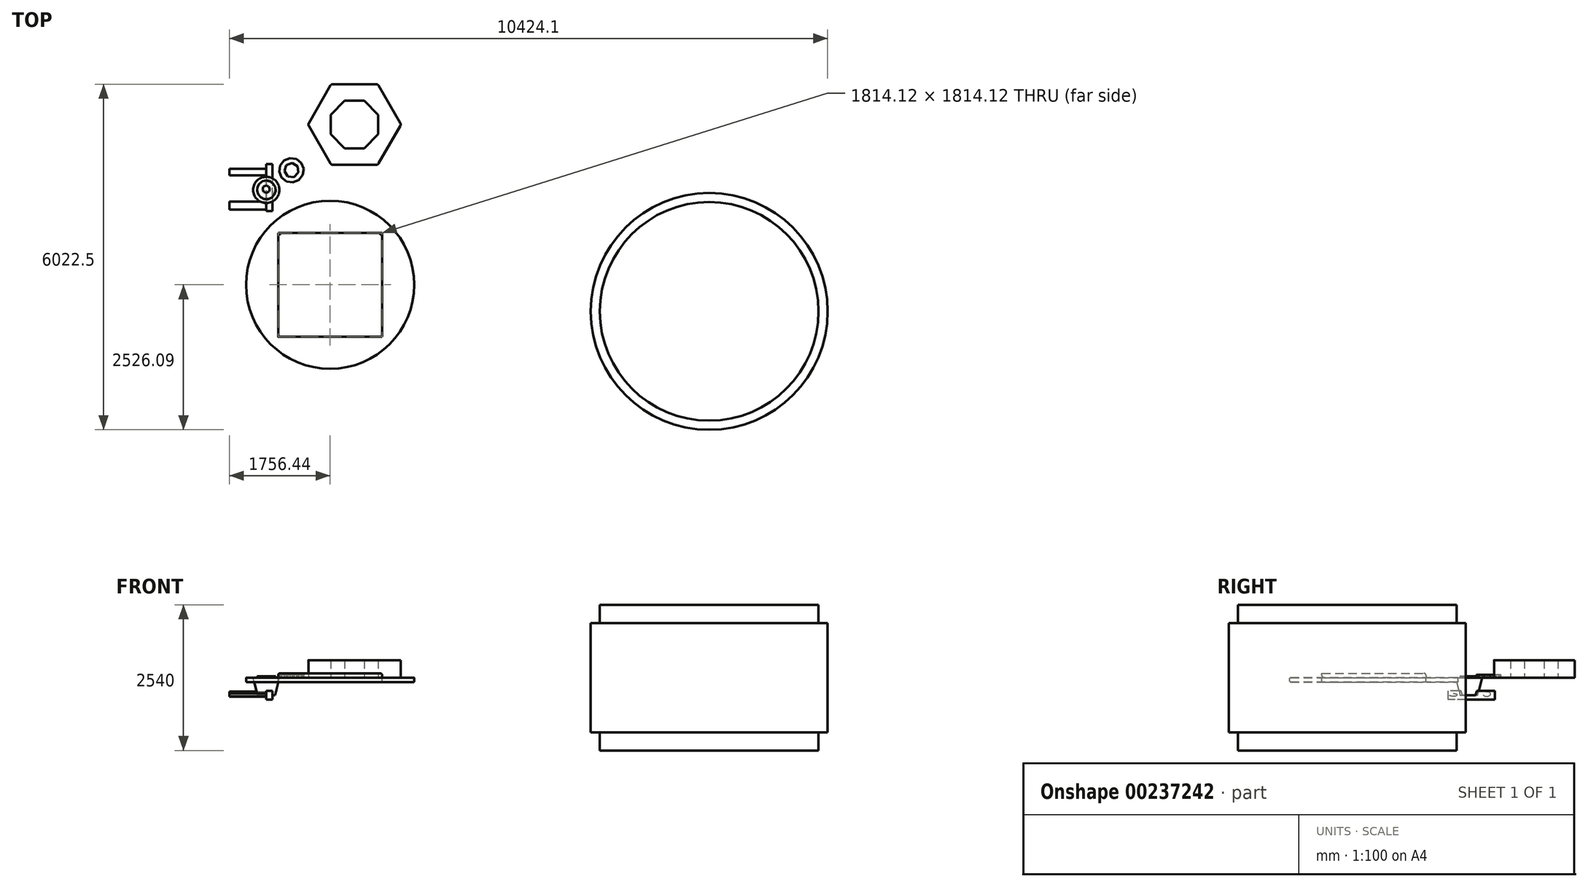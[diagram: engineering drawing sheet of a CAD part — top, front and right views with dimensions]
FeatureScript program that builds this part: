
annotation { "Feature Type Name" : "Feature", "Feature Type Description" : "" }
export const myFeature = defineFeature(function(context is Context, id is Id, definition is map)
    precondition{}
    {
        {
            var Q0;
            Q0=qCreatedBy(makeId("Top.planeOp"),FACE);
            var sketch = newSketch(context, id + "F0", { "sketchPlane" : qUnion([Q0])});
            skCircle(sketch, "E0.cCircle", {"center": v(0, 0) * mm, "radius": 162.75 * mm, "construction": true});
            skLineSegment(sketch, "E0.0", {"start": v(122.54, 107.1) * mm, "end": v(155.5, 48) * mm});
            skLineSegment(sketch, "E0.1", {"start": v(155.5, 48) * mm, "end": v(161.59, -19.4) * mm});
            skLineSegment(sketch, "E0.2", {"start": v(161.59, -19.4) * mm, "end": v(139.72, -83.45) * mm});
            skLineSegment(sketch, "E0.3", {"start": v(139.72, -83.45) * mm, "end": v(93.7, -133.07) * mm});
            skLineSegment(sketch, "E0.4", {"start": v(93.7, -133.07) * mm, "end": v(31.48, -159.67) * mm});
            skLineSegment(sketch, "E0.5", {"start": v(31.48, -159.67) * mm, "end": v(-36.19, -158.67) * mm});
            skLineSegment(sketch, "E0.6", {"start": v(-36.19, -158.67) * mm, "end": v(-97.6, -130.23) * mm});
            skLineSegment(sketch, "E0.7", {"start": v(-97.6, -130.23) * mm, "end": v(-142.13, -79.28) * mm});
            skLineSegment(sketch, "E0.8", {"start": v(-142.13, -79.28) * mm, "end": v(-162.09, -14.61) * mm});
            skLineSegment(sketch, "E0.9", {"start": v(-162.09, -14.61) * mm, "end": v(-154.02, 52.58) * mm});
            skLineSegment(sketch, "E0.10", {"start": v(-154.02, 52.58) * mm, "end": v(-119.32, 110.68) * mm});
            skLineSegment(sketch, "E0.11", {"start": v(-119.32, 110.68) * mm, "end": v(-63.99, 149.64) * mm});
            skLineSegment(sketch, "E0.12", {"start": v(-63.99, 149.64) * mm, "end": v(2.4, 162.73) * mm});
            skLineSegment(sketch, "E0.13", {"start": v(2.4, 162.73) * mm, "end": v(68.39, 147.68) * mm});
            skLineSegment(sketch, "E0.14", {"start": v(68.39, 147.68) * mm, "end": v(122.54, 107.1) * mm});
            skCircle(sketch, "E1.cCircle", {"center": v(0, 13.94) * mm, "radius": 64 * mm, "construction": true});
            skLineSegment(sketch, "E1.0", {"start": v(63.59, 21.28) * mm, "end": v(50.15, -25.83) * mm});
            skLineSegment(sketch, "E1.1", {"start": v(50.15, -25.83) * mm, "end": v(7.34, -49.65) * mm});
            skLineSegment(sketch, "E1.2", {"start": v(7.34, -49.65) * mm, "end": v(-39.77, -36.22) * mm});
            skLineSegment(sketch, "E1.3", {"start": v(-39.77, -36.22) * mm, "end": v(-63.59, 6.6) * mm});
            skLineSegment(sketch, "E1.4", {"start": v(-63.59, 6.6) * mm, "end": v(-50.15, 53.7) * mm});
            skLineSegment(sketch, "E1.5", {"start": v(-50.15, 53.7) * mm, "end": v(-7.34, 77.52) * mm});
            skLineSegment(sketch, "E1.6", {"start": v(-7.34, 77.52) * mm, "end": v(39.77, 64.09) * mm});
            skLineSegment(sketch, "E1.7", {"start": v(39.77, 64.09) * mm, "end": v(63.59, 21.28) * mm});
            skSolve(sketch);
        }
        {
            var Q0;
            Q0=makeQuery(id+"F0.imprint","IMPRINT",FACE,{"disambiguationData":[TD([[makeQuery(id+"F0.imprint","IMPRINT",EDGE,{"derivedFrom":sQuery(id+"F0.wireOp",EDGE,"E0.0")}),-1.0]])]});
            extrude(context, id + "F1", {"entities" : qUnion([Q0]), "depth" : 25.4 * mm});
        }
        {
            var Q0;
            Q0=qCreatedBy(makeId("Top.planeOp"),FACE);
            var sketch = newSketch(context, id + "F2", { "sketchPlane" : qUnion([Q0])});
            skCircle(sketch, "E2.cCircle", {"center": v(439.67, 342.5) * mm, "radius": 212.8 * mm, "construction": true});
            skLineSegment(sketch, "E2.0", {"start": v(635.27, 258.7) * mm, "end": v(567.16, 172.12) * mm});
            skLineSegment(sketch, "E2.1", {"start": v(567.16, 172.12) * mm, "end": v(464.89, 131.2) * mm});
            skLineSegment(sketch, "E2.2", {"start": v(464.89, 131.2) * mm, "end": v(355.86, 146.9) * mm});
            skLineSegment(sketch, "E2.3", {"start": v(355.86, 146.9) * mm, "end": v(269.29, 215.01) * mm});
            skLineSegment(sketch, "E2.4", {"start": v(269.29, 215.01) * mm, "end": v(228.37, 317.28) * mm});
            skLineSegment(sketch, "E2.5", {"start": v(228.37, 317.28) * mm, "end": v(244.07, 426.31) * mm});
            skLineSegment(sketch, "E2.6", {"start": v(244.07, 426.31) * mm, "end": v(312.18, 512.89) * mm});
            skLineSegment(sketch, "E2.7", {"start": v(312.18, 512.89) * mm, "end": v(414.45, 553.8) * mm});
            skLineSegment(sketch, "E2.8", {"start": v(414.45, 553.8) * mm, "end": v(523.48, 538.1) * mm});
            skLineSegment(sketch, "E2.9", {"start": v(523.48, 538.1) * mm, "end": v(610.05, 470) * mm});
            skLineSegment(sketch, "E2.10", {"start": v(610.05, 470) * mm, "end": v(650.97, 367.72) * mm});
            skLineSegment(sketch, "E2.11", {"start": v(650.97, 367.72) * mm, "end": v(635.27, 258.7) * mm});
            skCircle(sketch, "E3.cCircle", {"center": v(439.67, 342.5) * mm, "radius": 125.31 * mm, "construction": true});
            skLineSegment(sketch, "E3.0", {"start": v(558.33, 302.22) * mm, "end": v(482.16, 224.62) * mm});
            skLineSegment(sketch, "E3.1", {"start": v(482.16, 224.62) * mm, "end": v(374, 235.78) * mm});
            skLineSegment(sketch, "E3.2", {"start": v(374, 235.78) * mm, "end": v(315.28, 327.3) * mm});
            skLineSegment(sketch, "E3.3", {"start": v(315.28, 327.3) * mm, "end": v(350.23, 430.28) * mm});
            skLineSegment(sketch, "E3.4", {"start": v(350.23, 430.28) * mm, "end": v(452.53, 467.15) * mm});
            skLineSegment(sketch, "E3.5", {"start": v(452.53, 467.15) * mm, "end": v(545.14, 410.16) * mm});
            skLineSegment(sketch, "E3.6", {"start": v(545.14, 410.16) * mm, "end": v(558.33, 302.22) * mm});
            skSolve(sketch);
        }
        {
            var Q0;
            Q0=makeQuery(id+"F2.imprint","IMPRINT",FACE,{"disambiguationData":[TD([[makeQuery(id+"F2.imprint","IMPRINT",EDGE,{"derivedFrom":sQuery(id+"F2.wireOp",EDGE,"E2.0")}),-1.0]])]});
            extrude(context, id + "F3", {"entities" : qUnion([Q0]), "depth" : 51.3 * mm});
        }
        {
            var Q0;
            Q0=qCreatedBy(makeId("Top.planeOp"),FACE);
            var sketch = newSketch(context, id + "F4", { "sketchPlane" : qUnion([Q0])});
            skCircle(sketch, "E4.cCircle", {"center": v(1538.2, 1139.56) * mm, "radius": 810.97 * mm, "construction": true});
            skLineSegment(sketch, "E4.0", {"start": v(2349.16, 1139.56) * mm, "end": v(1943.68, 437.24) * mm});
            skLineSegment(sketch, "E4.1", {"start": v(1943.68, 437.24) * mm, "end": v(1132.71, 437.24) * mm});
            skLineSegment(sketch, "E4.2", {"start": v(1132.71, 437.24) * mm, "end": v(727.23, 1139.56) * mm});
            skLineSegment(sketch, "E4.3", {"start": v(727.23, 1139.56) * mm, "end": v(1132.71, 1841.87) * mm});
            skLineSegment(sketch, "E4.4", {"start": v(1132.71, 1841.87) * mm, "end": v(1943.68, 1841.87) * mm});
            skLineSegment(sketch, "E4.5", {"start": v(1943.68, 1841.87) * mm, "end": v(2349.16, 1139.56) * mm});
            skCircle(sketch, "E5.cCircle", {"center": v(1538.2, 1139.56) * mm, "radius": 447.1 * mm, "construction": true});
            skLineSegment(sketch, "E5.0", {"start": v(1951.26, 1310.66) * mm, "end": v(1951.26, 968.46) * mm});
            skLineSegment(sketch, "E5.1", {"start": v(1951.26, 968.46) * mm, "end": v(1709.3, 726.49) * mm});
            skLineSegment(sketch, "E5.2", {"start": v(1709.3, 726.49) * mm, "end": v(1367.1, 726.49) * mm});
            skLineSegment(sketch, "E5.3", {"start": v(1367.1, 726.49) * mm, "end": v(1125.13, 968.46) * mm});
            skLineSegment(sketch, "E5.4", {"start": v(1125.13, 968.46) * mm, "end": v(1125.13, 1310.66) * mm});
            skLineSegment(sketch, "E5.5", {"start": v(1125.13, 1310.66) * mm, "end": v(1367.1, 1552.63) * mm});
            skLineSegment(sketch, "E5.6", {"start": v(1367.1, 1552.63) * mm, "end": v(1709.3, 1552.63) * mm});
            skLineSegment(sketch, "E5.7", {"start": v(1709.3, 1552.63) * mm, "end": v(1951.26, 1310.66) * mm});
            skSolve(sketch);
        }
        {
            var Q0;
            Q0=makeQuery(id+"F4.imprint","IMPRINT",FACE,{"disambiguationData":[TD([[makeQuery(id+"F4.imprint","IMPRINT",EDGE,{"derivedFrom":sQuery(id+"F4.wireOp",EDGE,"E4.0")}),-1.0]])]});
            extrude(context, id + "F5", {"entities" : qUnion([Q0]), "depth" : 305.1 * mm});
        }
        {
            var Q0;
            Q0=makeQuery(id+"F5.opExtrude","SWEPT_EDGE",EDGE,{"disambiguationData":[OSD([sQuery(id+"F4.wireOp",EDGE,"E4.0"),sQuery(id+"F4.wireOp",EDGE,"E4.1")])]});
            var Q1;
            Q1=makeQuery(id+"F5.opExtrude","SWEPT_EDGE",EDGE,{"disambiguationData":[OSD([sQuery(id+"F4.wireOp",EDGE,"E4.0"),sQuery(id+"F4.wireOp",EDGE,"E4.5")])]});
            var Q2;
            Q2=makeQuery(id+"F5.opExtrude","SWEPT_EDGE",EDGE,{"disambiguationData":[OSD([sQuery(id+"F4.wireOp",EDGE,"E4.4"),sQuery(id+"F4.wireOp",EDGE,"E4.5")])]});
            var Q3;
            Q3=makeQuery(id+"F5.opExtrude","SWEPT_EDGE",EDGE,{"disambiguationData":[OSD([sQuery(id+"F4.wireOp",EDGE,"E4.3"),sQuery(id+"F4.wireOp",EDGE,"E4.4")])]});
            var Q4;
            Q4=makeQuery(id+"F5.opExtrude","SWEPT_EDGE",EDGE,{"disambiguationData":[OSD([sQuery(id+"F4.wireOp",EDGE,"E4.2"),sQuery(id+"F4.wireOp",EDGE,"E4.3")])]});
            var Q5;
            Q5=makeQuery(id+"F5.opExtrude","SWEPT_EDGE",EDGE,{"disambiguationData":[OSD([sQuery(id+"F4.wireOp",EDGE,"E4.1"),sQuery(id+"F4.wireOp",EDGE,"E4.2")])]});
            fillet(context, id + "F6", {"entities" : qUnion([Q0, Q1, Q2, Q3, Q4, Q5]), "radius" : 45.72 * mm, "tangentPropagation" : true, "allowEdgeOverflow" : false});
        }
        {
            var Q0;
            Q0=qCreatedBy(makeId("Top.planeOp"),FACE);
            var sketch = newSketch(context, id + "F7", { "sketchPlane" : qUnion([Q0])});
            skLineSegment(sketch, "E6.bottom", {"start": v(2020, -2561.6) * mm, "end": v(205.88, -2561.6) * mm});
            skLineSegment(sketch, "E6.top", {"start": v(2020, -747.49) * mm, "end": v(205.88, -747.49) * mm});
            skLineSegment(sketch, "E6.left", {"start": v(2020, -2561.6) * mm, "end": v(2020, -747.49) * mm});
            skLineSegment(sketch, "E6.right", {"start": v(205.88, -2561.6) * mm, "end": v(205.88, -747.49) * mm});
            skPoint(sketch, "E6.middle", {"position": v(1112.94, -1654.54) * mm});
            skCircle(sketch, "E7", {"center": v(1112.94, -1654.54) * mm, "radius": 1465.04 * mm});
            skSolve(sketch);
        }
        {
            var Q0;
            Q0=makeQuery(id+"F7.imprint","IMPRINT",FACE,{"disambiguationData":[TD([[makeQuery(id+"F7.imprint","IMPRINT",EDGE,{"derivedFrom":sQuery(id+"F7.wireOp",EDGE,"E6.bottom")}),1.0]])]});
            extrude(context, id + "F8", {"entities" : qUnion([Q0]), "oppositeDirection" : true, "depth" : 76.2 * mm});
        }
        {
            var Q0;
            Q0=makeQuery(id+"F7.imprint","IMPRINT",FACE,{"disambiguationData":[TD([[makeQuery(id+"F7.imprint","IMPRINT",EDGE,{"derivedFrom":sQuery(id+"F7.wireOp",EDGE,"E6.bottom")}),-1.0]])]});
            extrude(context, id + "F9", {"entities" : qUnion([Q0]), "depth" : 76.2 * mm});
        }
        {
            var Q0;
            Q0=makeQuery(id+"F9.opExtrude","CAP_EDGE",EDGE,{"disambiguationData":[OSD([sQuery(id+"F7.wireOp",EDGE,"E6.right")])],"isStart":false});
            var Q1;
            Q1=makeQuery(id+"F9.opExtrude","CAP_EDGE",EDGE,{"disambiguationData":[OSD([sQuery(id+"F7.wireOp",EDGE,"E6.left")])],"isStart":false});
            var Q2;
            Q2=makeQuery(id+"F9.opExtrude","CAP_EDGE",EDGE,{"disambiguationData":[OSD([sQuery(id+"F7.wireOp",EDGE,"E6.bottom")])],"isStart":true});
            var Q3;
            Q3=makeQuery(id+"F9.opExtrude","CAP_EDGE",EDGE,{"disambiguationData":[OSD([sQuery(id+"F7.wireOp",EDGE,"E6.top")])],"isStart":false});
            fillet(context, id + "F10", {"entities" : qUnion([Q0, Q1, Q2, Q3]), "radius" : 38.1 * mm, "tangentPropagation" : true, "allowEdgeOverflow" : false});
        }
        {
            var Q0;
            Q0=makeQuery(id+"F8.opExtrude","CAP_EDGE",EDGE,{"disambiguationData":[OSD([sQuery(id+"F7.wireOp",EDGE,"E7")])],"isStart":true});
            var Q1;
            Q1=makeQuery(id+"F8.opExtrude","CAP_EDGE",EDGE,{"disambiguationData":[OSD([sQuery(id+"F7.wireOp",EDGE,"E7")])],"isStart":false});
            fillet(context, id + "F11", {"entities" : qUnion([Q0, Q1]), "radius" : 12.7 * mm, "tangentPropagation" : true, "allowEdgeOverflow" : false});
        }
        {
            var Q0;
            Q0=qCreatedBy(makeId("Top.planeOp"),FACE);
            var sketch = newSketch(context, id + "F12", { "sketchPlane" : qUnion([Q0])});
            skCircle(sketch, "E8", {"center": v(7716.86, -2116.88) * mm, "radius": 1905 * mm});
            skCircle(sketch, "E9", {"center": v(7716.86, -2116.88) * mm, "radius": 2063.75 * mm});
            skSolve(sketch);
        }
        {
            var Q0;
            Q0=makeQuery(id+"F12.imprint","IMPRINT",FACE,{"disambiguationData":[TD([[makeQuery(id+"F12.imprint","IMPRINT",EDGE,{"derivedFrom":sQuery(id+"F12.wireOp",EDGE,"E8")}),1.0]])]});
            extrude(context, id + "F13", {"entities" : qUnion([Q0]), "endBound" : BoundingType.SYMMETRIC, "depth" : 2540 * mm});
        }
        {
            var Q0;
            Q0=makeQuery(id+"F12.imprint","IMPRINT",FACE,{"disambiguationData":[TD([[makeQuery(id+"F12.imprint","IMPRINT",EDGE,{"derivedFrom":sQuery(id+"F12.wireOp",EDGE,"E8")}),-1.0]])]});
            extrude(context, id + "F14", {"entities" : qUnion([Q0]), "operationType" : NewBodyOperationType.ADD, "endBound" : BoundingType.SYMMETRIC, "depth" : 1905 * mm});
        }
        {
            var Q0;
            Q0=qCreatedBy(makeId("Top.planeOp"),FACE);
            cPlane(context, id + "F15", {"entities" : qUnion([Q0]), "cplaneType" : CPlaneType.OFFSET, "offset" : 304.8 * mm, "width" : 152.4 * mm, "height" : 152.4 * mm});
        }
        {
            var Q0;
            Q0=qCreatedBy(id+"F15.planeOp",FACE);
            var sketch = newSketch(context, id + "F16", { "sketchPlane" : qUnion([Q0])});
            skCircle(sketch, "E10", {"center": v(0, 0) * mm, "radius": 59.05 * mm});
            skSolve(sketch);
        }
        {
            var Q0;
            Q0=qCreatedBy(makeId("Top.planeOp"),FACE);
            var sketch = newSketch(context, id + "F17", { "sketchPlane" : qUnion([Q0])});
            skCircle(sketch, "E11", {"center": v(7.21, 0) * mm, "radius": 135.16 * mm});
            skSolve(sketch);
        }
        {
            var Q0;
            Q0=makeQuery(id+"F17.imprint","IMPRINT",FACE,{"disambiguationData":[TD([[makeQuery(id+"F17.imprint","IMPRINT",EDGE,{"derivedFrom":sQuery(id+"F17.wireOp",EDGE,"E11")}),1.0]])]});
            var Q1;
            Q1=sQuery(id+"F17.wireOp",EDGE,"E11");
            var Q2;
            Q2=sQuery(id+"F16.wireOp",EDGE,"E10");
            loft(context, id + "F18", {"bodyType" : ToolBodyType.SURFACE, "sheetProfilesArray" : [{ "sheetProfileEntities" : qUnion([Q0]) }], "wireProfilesArray" : [{ "wireProfileEntities" : qUnion([Q1]) }, { "wireProfileEntities" : qUnion([Q2]) }]});
        }
        {
            var Q0;
            Q0=qCreatedBy(makeId("Top.planeOp"),FACE);
            var sketch = newSketch(context, id + "F19", { "sketchPlane" : qUnion([Q0])});
            skCircle(sketch, "E12", {"center": v(0, 0) * mm, "radius": 229.08 * mm});
            skSolve(sketch);
        }
        {
            var Q0;
            Q0=qCreatedBy(makeId("Top.planeOp"),FACE);
            cPlane(context, id + "F20", {"entities" : qUnion([Q0]), "cplaneType" : CPlaneType.OFFSET, "offset" : 304.8 * mm, "oppositeDirection" : true, "width" : 152.4 * mm, "height" : 152.4 * mm});
        }
        {
            var Q0;
            Q0=qCreatedBy(id+"F20.planeOp",FACE);
            var sketch = newSketch(context, id + "F21", { "sketchPlane" : qUnion([Q0])});
            skCircle(sketch, "E13", {"center": v(0, 0) * mm, "radius": 154.64 * mm});
            skSolve(sketch);
        }
        {
            var Q0;
            Q0=makeQuery(id+"F19.imprint","IMPRINT",FACE,{"disambiguationData":[TD([[makeQuery(id+"F19.imprint","IMPRINT",EDGE,{"derivedFrom":sQuery(id+"F19.wireOp",EDGE,"E12")}),1.0]])]});
            var Q1;
            Q1=makeQuery(id+"F21.imprint","IMPRINT",FACE,{"disambiguationData":[TD([[makeQuery(id+"F21.imprint","IMPRINT",EDGE,{"derivedFrom":sQuery(id+"F21.wireOp",EDGE,"E13")}),1.0]])]});
            loft(context, id + "F22", {"sheetProfilesArray" : [{ "sheetProfileEntities" : qUnion([Q0]) }, { "sheetProfileEntities" : qUnion([Q1]) }]});
        }
        {
            var Q0;
            Q0=qCreatedBy(id+"F20.planeOp",FACE);
            var sketch = newSketch(context, id + "F23", { "sketchPlane" : qUnion([Q0])});
            skLineSegment(sketch, "E14.bottom", {"start": v(0, 449.05) * mm, "end": v(104.81, 449.05) * mm});
            skLineSegment(sketch, "E14.top", {"start": v(0, -367.79) * mm, "end": v(104.81, -367.79) * mm});
            skLineSegment(sketch, "E14.left", {"start": v(0, 449.05) * mm, "end": v(0, -367.79) * mm});
            skLineSegment(sketch, "E14.right", {"start": v(104.81, 449.05) * mm, "end": v(104.81, -367.79) * mm});
            skPoint(sketch, "E14.middle", {"position": v(52.4, 40.63) * mm});
            skSolve(sketch);
        }
        {
            var Q0;
            Q0=qSketchRegion(id+"F23",true);
            extrude(context, id + "F24", {"entities" : qUnion([Q0]), "operationType" : NewBodyOperationType.ADD, "endBound" : BoundingType.SYMMETRIC, "depth" : 152.4 * mm});
        }
        {
            var Q0;
            Q0=makeQuery(id+"F24.opExtrude","SWEPT_FACE",FACE,{"disambiguationData":[OSD([sQuery(id+"F23.wireOp",EDGE,"E14.left")])]});
            var sketch = newSketch(context, id + "F25", { "sketchPlane" : qUnion([Q0])});
            skEllipse(sketch, "E15", {"center": v(272.7, -302.16) * mm, "majorRadius": 68.02 * mm, "minorRadius": 24.74 * mm, "majorAxis": v(-1, 0)});
            skEllipse(sketch, "E16", {"center": v(-310.37, -287.26) * mm, "majorRadius": 59.3 * mm, "minorRadius": 46.6 * mm, "majorAxis": v(-1, 0)});
            skSolve(sketch);
        }
        {
            var Q0;
            Q0=qSketchRegion(id+"F25",true);
            extrude(context, id + "F26", {"entities" : qUnion([Q0]), "operationType" : NewBodyOperationType.ADD, "depth" : 643.5 * mm});
        }
    });
